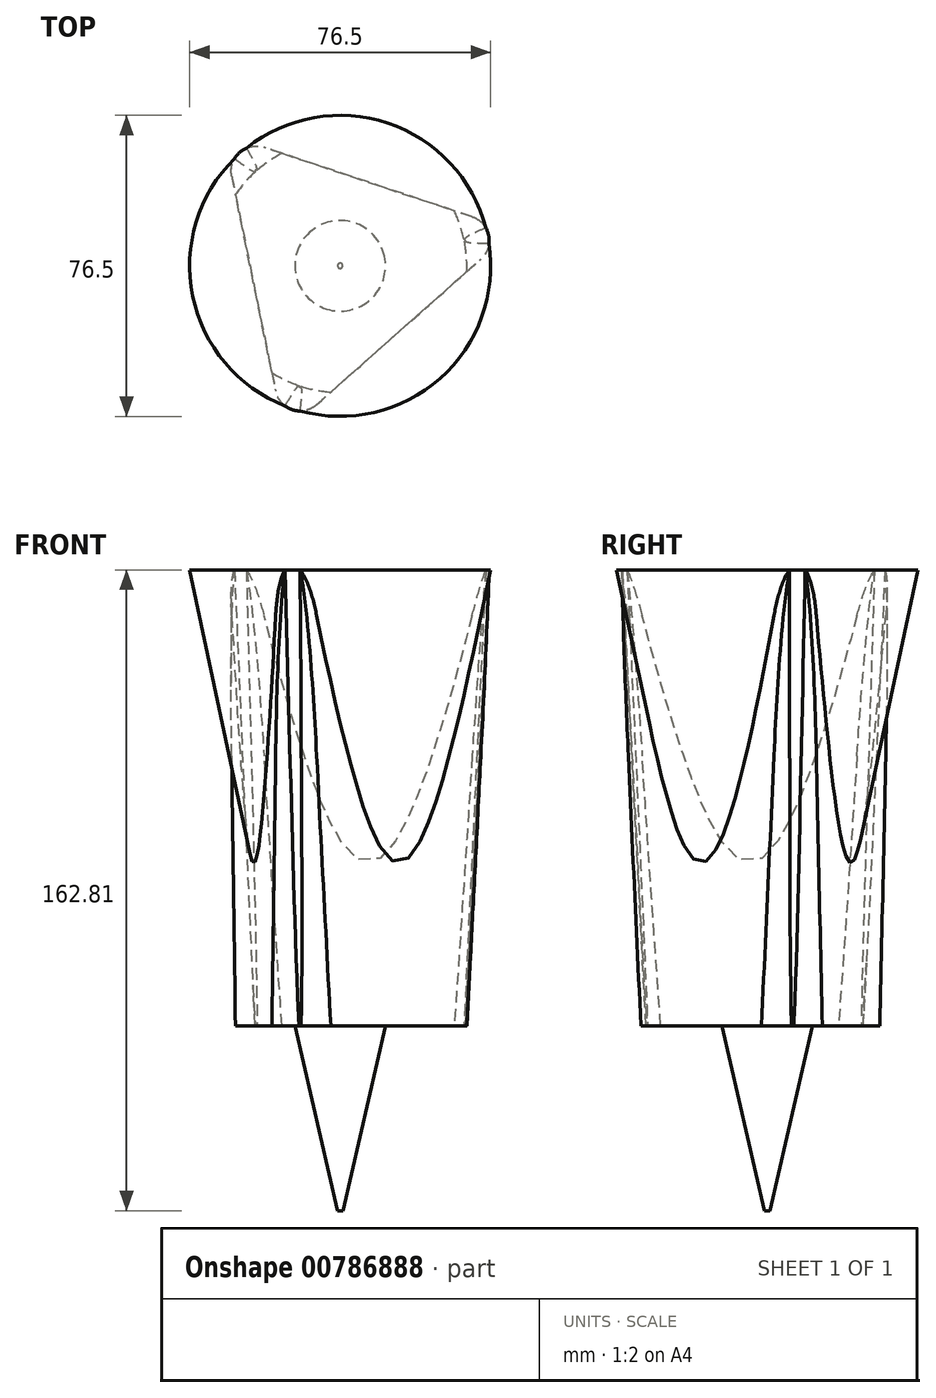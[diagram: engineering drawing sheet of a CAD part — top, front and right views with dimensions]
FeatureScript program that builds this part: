
annotation { "Feature Type Name" : "Feature", "Feature Type Description" : "" }
export const myFeature = defineFeature(function(context is Context, id is Id, definition is map)
    precondition{}
    {
        {
            var Q0;
            Q0=qCreatedBy(makeId("Top.planeOp"),FACE);
            var sketch = newSketch(context, id + "F0", { "sketchPlane" : qUnion([Q0])});
            skCircle(sketch, "E0.cCircle", {"center": v(0, 0) * mm, "radius": 22.44 * mm, "construction": true});
            skLineSegment(sketch, "E0.0", {"start": v(-19.34, 30.1) * mm, "end": v(33.53, 12.47) * mm});
            skLineSegment(sketch, "E0.1", {"start": v(35.73, 1.7) * mm, "end": v(-5.96, -35.27) * mm});
            skLineSegment(sketch, "E0.2", {"start": v(-16.4, -31.8) * mm, "end": v(-27.57, 22.8) * mm});
            skPoint(sketch, "E0.0.midPoint", {"position": v(7.1, 21.28) * mm});
            skPoint(sketch, "E1.visualSharp", {"position": v(-29.77, 33.57) * mm});
            skArc(sketch, "E1.filletArc", {"start": v(-19.34, 30.1) * mm, "mid": v(-25.56, 28.82) * mm, "end": v(-27.57, 22.8) * mm});
            skPoint(sketch, "E2.visualSharp", {"position": v(43.96, 9) * mm});
            skArc(sketch, "E2.filletArc", {"start": v(35.73, 1.7) * mm, "mid": v(37.74, 7.72) * mm, "end": v(33.53, 12.47) * mm});
            skPoint(sketch, "E3.visualSharp", {"position": v(-14.19, -42.57) * mm});
            skArc(sketch, "E3.filletArc", {"start": v(-16.4, -31.8) * mm, "mid": v(-12.18, -36.55) * mm, "end": v(-5.96, -35.27) * mm});
            skSolve(sketch);
        }
        {
            var Q0;
            Q0=makeQuery(id+"F0.imprint","IMPRINT",FACE,{"disambiguationData":[TD([[makeQuery(id+"F0.imprint","IMPRINT",EDGE,{"derivedFrom":sQuery(id+"F0.wireOp",EDGE,"E0.0")}),-1.0]])]});
            extrude(context, id + "F1", {"entities" : qUnion([Q0]), "depth" : 149.86 * mm, "offsetDistance" : 25.4 * mm});
        }
        {
            var Q0;
            Q0=makeQuery(id+"F1.opExtrude","CAP_FACE",FACE,{"disambiguationData":[OSD([sQuery(id+"F0.wireOp",EDGE,"E0.0"),sQuery(id+"F0.wireOp",EDGE,"E0.1"),sQuery(id+"F0.wireOp",EDGE,"E0.2"),sQuery(id+"F0.wireOp",EDGE,"E1.filletArc"),sQuery(id+"F0.wireOp",EDGE,"E2.filletArc"),sQuery(id+"F0.wireOp",EDGE,"E3.filletArc")])],"isStart":false});
            var sketch = newSketch(context, id + "F2", { "sketchPlane" : qUnion([Q0])});
            skCircle(sketch, "E4", {"center": v(0, 0) * mm, "radius": 38.25 * mm});
            skSolve(sketch);
        }
        {
            var Q0;
            Q0 = qSketchRegion(id + "F2", true);
            extrude(context, id + "F3", {"entities" : qUnion([Q0]), "operationType" : NewBodyOperationType.ADD, "oppositeDirection" : true, "depth" : 187.7 * mm, "offsetDistance" : 25.4 * mm, "hasDraft" : true, "draftAngle" : 12 * degree, "draftPullDirection" : true});
        }
        {
            var Q0;
            Q0=makeQuery(id+"F3.boolean.opBoolean","MERGE",FACE,{"derivedFrom":[makeQuery(id+"F1.opExtrude","CAP_FACE",FACE,{"disambiguationData":[OSD([sQuery(id+"F0.wireOp",EDGE,"E0.0"),sQuery(id+"F0.wireOp",EDGE,"E0.1"),sQuery(id+"F0.wireOp",EDGE,"E0.2"),sQuery(id+"F0.wireOp",EDGE,"E1.filletArc"),sQuery(id+"F0.wireOp",EDGE,"E2.filletArc"),sQuery(id+"F0.wireOp",EDGE,"E3.filletArc")])],"isStart":false}),makeQuery(id+"F3.opExtrude","CAP_FACE",FACE,{"disambiguationData":[OSD([sQuery(id+"F2.wireOp",EDGE,"E4")])],"isStart":true})]});
            extrude(context, id + "F4", {"entities" : qUnion([Q0]), "operationType" : NewBodyOperationType.INTERSECT, "oppositeDirection" : true, "depth" : 115.82 * mm, "offsetDistance" : 25.4 * mm, "hasDraft" : true, "draftAngle" : 15 * degree});
        }
        {
            var Q0;
            Q0=makeQuery(id+"F3.boolean.opBoolean","MERGE",FACE,{"derivedFrom":[makeQuery(id+"F1.opExtrude","CAP_FACE",FACE,{"disambiguationData":[OSD([sQuery(id+"F0.wireOp",EDGE,"E0.0"),sQuery(id+"F0.wireOp",EDGE,"E0.1"),sQuery(id+"F0.wireOp",EDGE,"E0.2"),sQuery(id+"F0.wireOp",EDGE,"E1.filletArc"),sQuery(id+"F0.wireOp",EDGE,"E2.filletArc"),sQuery(id+"F0.wireOp",EDGE,"E3.filletArc")])],"isStart":false}),makeQuery(id+"F3.opExtrude","CAP_FACE",FACE,{"disambiguationData":[OSD([sQuery(id+"F2.wireOp",EDGE,"E4")])],"isStart":true})]});
            extrude(context, id + "F5", {"entities" : qUnion([Q0]), "operationType" : NewBodyOperationType.ADD, "oppositeDirection" : true, "depth" : 162.8 * mm, "offsetDistance" : 25.4 * mm, "hasDraft" : true, "draftAngle" : 13 * degree, "draftPullDirection" : true});
        }
        {
            var Q0;
            Q0=makeQuery(id+"F3.boolean.opBoolean","MERGE",FACE,{"derivedFrom":[makeQuery(id+"F1.opExtrude","CAP_FACE",FACE,{"disambiguationData":[OSD([sQuery(id+"F0.wireOp",EDGE,"E0.0"),sQuery(id+"F0.wireOp",EDGE,"E0.1"),sQuery(id+"F0.wireOp",EDGE,"E0.2"),sQuery(id+"F0.wireOp",EDGE,"E1.filletArc"),sQuery(id+"F0.wireOp",EDGE,"E2.filletArc"),sQuery(id+"F0.wireOp",EDGE,"E3.filletArc")])],"isStart":false}),makeQuery(id+"F3.opExtrude","CAP_FACE",FACE,{"disambiguationData":[OSD([sQuery(id+"F2.wireOp",EDGE,"E4")])],"isStart":true})]});
            extrude(context, id + "F6", {"entities" : qUnion([Q0]), "operationType" : NewBodyOperationType.INTERSECT, "oppositeDirection" : true, "depth" : 190 * mm, "offsetDistance" : 25.4 * mm, "hasDraft" : true, "draftAngle" : 3 * degree, "draftPullDirection" : true});
        }
    });
